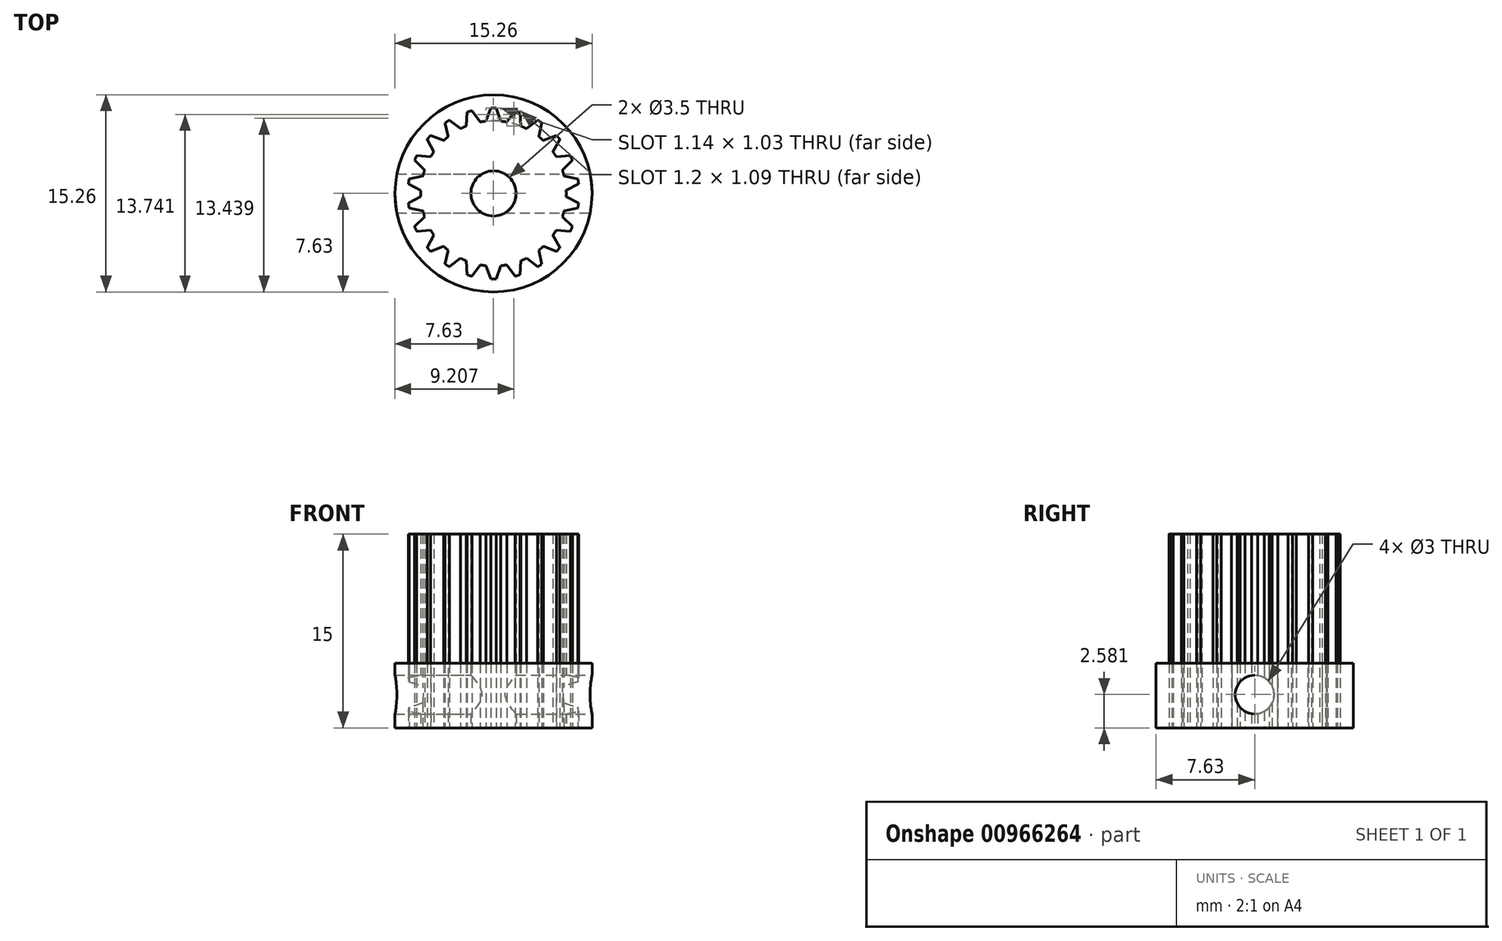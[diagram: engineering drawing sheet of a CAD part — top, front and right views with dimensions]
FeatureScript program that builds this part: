
annotation { "Feature Type Name" : "Feature", "Feature Type Description" : "" }
export const myFeature = defineFeature(function(context is Context, id is Id, definition is map)
    precondition{}
    {
        {
            var Q0;
            Q0=qCreatedBy(makeId("Top.planeOp"),FACE);
            var sketch = newSketch(context, id + "F0", { "sketchPlane" : qUnion([Q0])});
            skCircle(sketch, "E0", {"center": v(0, 0) * mm, "radius": 5.62 * mm});
            skCircle(sketch, "E1", {"center": v(0, 0) * mm, "radius": 7.12 * mm});
            skLineSegment(sketch, "E2", {"start": v(-0.01, 7.12) * mm, "end": v(-0.2, 6.62) * mm});
            skLineSegment(sketch, "E3", {"start": v(0.01, 7.12) * mm, "end": v(0.57, 5.6) * mm});
            skLineSegment(sketch, "E4.1.0", {"start": v(-2.02, 6.83) * mm, "end": v(-2.12, 5.2) * mm});
            skLineSegment(sketch, "E4.1.1", {"start": v(-2, 6.84) * mm, "end": v(-1.03, 5.53) * mm});
            skLineSegment(sketch, "E4.2.0", {"start": v(-3.86, 5.99) * mm, "end": v(-3.5, 4.4) * mm});
            skLineSegment(sketch, "E4.2.1", {"start": v(-3.84, 6) * mm, "end": v(-2.55, 5.02) * mm});
            skLineSegment(sketch, "E4.3.0", {"start": v(-5.4, 4.66) * mm, "end": v(-4.6, 3.23) * mm});
            skLineSegment(sketch, "E4.3.1", {"start": v(-5.38, 4.68) * mm, "end": v(-3.86, 4.1) * mm});
            skLineSegment(sketch, "E4.4.0", {"start": v(-6.49, 2.95) * mm, "end": v(-5.33, 1.8) * mm});
            skLineSegment(sketch, "E4.4.1", {"start": v(-6.48, 2.97) * mm, "end": v(-4.85, 2.84) * mm});
            skLineSegment(sketch, "E4.5.0", {"start": v(-7.05, 1) * mm, "end": v(-5.62, 0.23) * mm});
            skLineSegment(sketch, "E4.5.1", {"start": v(-7.05, 1.03) * mm, "end": v(-5.46, 1.36) * mm});
            skLineSegment(sketch, "E4.6.0", {"start": v(-7.05, -1.03) * mm, "end": v(-5.46, -1.36) * mm});
            skLineSegment(sketch, "E4.6.1", {"start": v(-7.05, -1) * mm, "end": v(-5.62, -0.23) * mm});
            skLineSegment(sketch, "E4.7.0", {"start": v(-6.48, -2.97) * mm, "end": v(-4.85, -2.84) * mm});
            skLineSegment(sketch, "E4.7.1", {"start": v(-6.49, -2.95) * mm, "end": v(-5.33, -1.8) * mm});
            skLineSegment(sketch, "E4.8.0", {"start": v(-5.38, -4.68) * mm, "end": v(-3.86, -4.1) * mm});
            skLineSegment(sketch, "E4.8.1", {"start": v(-5.4, -4.66) * mm, "end": v(-4.6, -3.23) * mm});
            skLineSegment(sketch, "E4.9.0", {"start": v(-3.84, -6) * mm, "end": v(-2.55, -5.02) * mm});
            skLineSegment(sketch, "E4.9.1", {"start": v(-3.86, -5.99) * mm, "end": v(-3.5, -4.4) * mm});
            skLineSegment(sketch, "E5.2.10.0", {"start": v(-2, -6.84) * mm, "end": v(-1.03, -5.53) * mm});
            skLineSegment(sketch, "E5.3.10.0", {"start": v(-2.02, -6.83) * mm, "end": v(-2.12, -5.2) * mm});
            skLineSegment(sketch, "E5.2.11.0", {"start": v(0.01, -7.12) * mm, "end": v(0.57, -5.6) * mm});
            skLineSegment(sketch, "E5.3.11.0", {"start": v(-0.01, -7.12) * mm, "end": v(-0.57, -5.6) * mm});
            skLineSegment(sketch, "E5.2.12.0", {"start": v(2.02, -6.83) * mm, "end": v(2.12, -5.2) * mm});
            skLineSegment(sketch, "E5.3.12.0", {"start": v(2, -6.84) * mm, "end": v(1.03, -5.53) * mm});
            skLineSegment(sketch, "E5.2.13.0", {"start": v(3.86, -5.99) * mm, "end": v(3.5, -4.4) * mm});
            skLineSegment(sketch, "E5.3.13.0", {"start": v(3.84, -6) * mm, "end": v(2.55, -5.02) * mm});
            skLineSegment(sketch, "E5.2.14.0", {"start": v(5.4, -4.66) * mm, "end": v(4.6, -3.23) * mm});
            skLineSegment(sketch, "E5.3.14.0", {"start": v(5.38, -4.68) * mm, "end": v(3.86, -4.1) * mm});
            skLineSegment(sketch, "E5.2.15.0", {"start": v(6.49, -2.95) * mm, "end": v(5.33, -1.8) * mm});
            skLineSegment(sketch, "E5.3.15.0", {"start": v(6.48, -2.97) * mm, "end": v(4.85, -2.84) * mm});
            skLineSegment(sketch, "E5.2.16.0", {"start": v(7.05, -1) * mm, "end": v(5.62, -0.23) * mm});
            skLineSegment(sketch, "E5.3.16.0", {"start": v(7.05, -1.03) * mm, "end": v(5.46, -1.36) * mm});
            skLineSegment(sketch, "E5.2.17.0", {"start": v(7.05, 1.03) * mm, "end": v(5.46, 1.36) * mm});
            skLineSegment(sketch, "E5.3.17.0", {"start": v(7.05, 1) * mm, "end": v(5.62, 0.23) * mm});
            skLineSegment(sketch, "E5.2.18.0", {"start": v(6.48, 2.97) * mm, "end": v(4.85, 2.84) * mm});
            skLineSegment(sketch, "E5.3.18.0", {"start": v(6.49, 2.95) * mm, "end": v(5.33, 1.8) * mm});
            skLineSegment(sketch, "E5.2.19.0", {"start": v(5.38, 4.68) * mm, "end": v(3.86, 4.1) * mm});
            skLineSegment(sketch, "E5.3.19.0", {"start": v(5.4, 4.66) * mm, "end": v(4.6, 3.23) * mm});
            skLineSegment(sketch, "E6.2.20.0", {"start": v(3.84, 6) * mm, "end": v(2.55, 5.02) * mm});
            skLineSegment(sketch, "E6.3.20.0", {"start": v(3.86, 5.99) * mm, "end": v(3.5, 4.4) * mm});
            skCircle(sketch, "E7", {"center": v(0, 0) * mm, "radius": 1.75 * mm});
            skCircle(sketch, "E8", {"center": v(0, 0) * mm, "radius": 7.62 * mm});
            skLineSegment(sketch, "E9.2.21.0", {"start": v(2, 6.84) * mm, "end": v(1.03, 5.53) * mm});
            skLineSegment(sketch, "E9.3.21.0", {"start": v(2.02, 6.83) * mm, "end": v(2.12, 5.2) * mm});
            skLineSegment(sketch, "E10", {"start": v(-0.2, 6.62) * mm, "end": v(-0.57, 5.6) * mm});
            skArc(sketch, "E11", {"start": v(0.2, 6.62) * mm, "mid": v(0, 6.63) * mm, "end": v(-0.2, 6.62) * mm});
            skArc(sketch, "E12", {"start": v(-0.2, 6.62) * mm, "mid": v(0, -6.63) * mm, "end": v(0.2, 6.62) * mm});
            skSolve(sketch);
        }
        {
            var Q0;
            Q0=makeQuery(id+"F0.imprint","IMPRINT",FACE,{"disambiguationData":[TD([[makeQuery(id+"F0.imprint","IMPRINT",EDGE,{"derivedFrom":sQuery(id+"F0.wireOp",EDGE,"E7")}),-1.0]])]});
            var Q1;
            {var subQ3=sQuery(id+"F0.wireOp",EDGE,"E10");Q1=makeQuery(id+"F0.imprint","IMPRINT",FACE,{"disambiguationData":[TD([[makeQuery(id+"F0.imprint","IMPRINT",EDGE,{"derivedFrom":subQ3}),1.0]])]});}
            var Q2;
            {var subQ0=sQuery(id+"F0.wireOp",EDGE,"E9.2.21.0");var subQ1=sQuery(id+"F0.wireOp",EDGE,"E0");var subQ2=makeQuery(id+"F0.imprint","INTERSECT",VERTEX,{"derivedFrom":[subQ1,subQ0]});Q2=makeQuery(id+"F0.imprint","IMPRINT",FACE,{"disambiguationData":[TD([[makeQuery(id+"F0.imprint","IMPRINT",EDGE,{"disambiguationData":[TD([[subQ2,1.0]])],"derivedFrom":subQ1}),-1.0]])]});}
            var Q3;
            {var subQ0=sQuery(id+"F0.wireOp",EDGE,"E6.2.20.0");var subQ1=sQuery(id+"F0.wireOp",EDGE,"E0");var subQ2=makeQuery(id+"F0.imprint","INTERSECT",VERTEX,{"derivedFrom":[subQ1,subQ0]});Q3=makeQuery(id+"F0.imprint","IMPRINT",FACE,{"disambiguationData":[TD([[makeQuery(id+"F0.imprint","IMPRINT",EDGE,{"disambiguationData":[TD([[subQ2,1.0]])],"derivedFrom":subQ1}),-1.0]])]});}
            var Q4;
            {var subQ0=sQuery(id+"F0.wireOp",EDGE,"E5.2.19.0");var subQ1=sQuery(id+"F0.wireOp",EDGE,"E0");var subQ2=makeQuery(id+"F0.imprint","INTERSECT",VERTEX,{"derivedFrom":[subQ1,subQ0]});Q4=makeQuery(id+"F0.imprint","IMPRINT",FACE,{"disambiguationData":[TD([[makeQuery(id+"F0.imprint","IMPRINT",EDGE,{"disambiguationData":[TD([[subQ2,1.0]])],"derivedFrom":subQ1}),-1.0]])]});}
            var Q5;
            {var subQ0=sQuery(id+"F0.wireOp",EDGE,"E5.2.18.0");var subQ1=sQuery(id+"F0.wireOp",EDGE,"E0");var subQ2=makeQuery(id+"F0.imprint","INTERSECT",VERTEX,{"derivedFrom":[subQ1,subQ0]});Q5=makeQuery(id+"F0.imprint","IMPRINT",FACE,{"disambiguationData":[TD([[makeQuery(id+"F0.imprint","IMPRINT",EDGE,{"disambiguationData":[TD([[subQ2,1.0]])],"derivedFrom":subQ1}),-1.0]])]});}
            var Q6;
            {var subQ0=sQuery(id+"F0.wireOp",EDGE,"E5.2.17.0");var subQ1=sQuery(id+"F0.wireOp",EDGE,"E0");var subQ2=makeQuery(id+"F0.imprint","INTERSECT",VERTEX,{"derivedFrom":[subQ1,subQ0]});Q6=makeQuery(id+"F0.imprint","IMPRINT",FACE,{"disambiguationData":[TD([[makeQuery(id+"F0.imprint","IMPRINT",EDGE,{"disambiguationData":[TD([[subQ2,1.0]])],"derivedFrom":subQ1}),-1.0]])]});}
            var Q7;
            {var subQ0=sQuery(id+"F0.wireOp",EDGE,"E5.2.16.0");var subQ1=sQuery(id+"F0.wireOp",EDGE,"E0");var subQ2=makeQuery(id+"F0.imprint","INTERSECT",VERTEX,{"derivedFrom":[subQ1,subQ0]});Q7=makeQuery(id+"F0.imprint","IMPRINT",FACE,{"disambiguationData":[TD([[makeQuery(id+"F0.imprint","IMPRINT",EDGE,{"disambiguationData":[TD([[subQ2,1.0]])],"derivedFrom":subQ1}),-1.0]])]});}
            var Q8;
            {var subQ0=sQuery(id+"F0.wireOp",EDGE,"E5.2.15.0");var subQ1=sQuery(id+"F0.wireOp",EDGE,"E0");var subQ2=makeQuery(id+"F0.imprint","INTERSECT",VERTEX,{"derivedFrom":[subQ1,subQ0]});Q8=makeQuery(id+"F0.imprint","IMPRINT",FACE,{"disambiguationData":[TD([[makeQuery(id+"F0.imprint","IMPRINT",EDGE,{"disambiguationData":[TD([[subQ2,1.0]])],"derivedFrom":subQ1}),-1.0]])]});}
            var Q9;
            {var subQ0=sQuery(id+"F0.wireOp",EDGE,"E5.2.14.0");var subQ1=sQuery(id+"F0.wireOp",EDGE,"E0");var subQ2=makeQuery(id+"F0.imprint","INTERSECT",VERTEX,{"derivedFrom":[subQ1,subQ0]});Q9=makeQuery(id+"F0.imprint","IMPRINT",FACE,{"disambiguationData":[TD([[makeQuery(id+"F0.imprint","IMPRINT",EDGE,{"disambiguationData":[TD([[subQ2,1.0]])],"derivedFrom":subQ1}),-1.0]])]});}
            var Q10;
            {var subQ0=sQuery(id+"F0.wireOp",EDGE,"E5.2.13.0");var subQ1=sQuery(id+"F0.wireOp",EDGE,"E0");var subQ2=makeQuery(id+"F0.imprint","INTERSECT",VERTEX,{"derivedFrom":[subQ1,subQ0]});Q10=makeQuery(id+"F0.imprint","IMPRINT",FACE,{"disambiguationData":[TD([[makeQuery(id+"F0.imprint","IMPRINT",EDGE,{"disambiguationData":[TD([[subQ2,1.0]])],"derivedFrom":subQ1}),-1.0]])]});}
            var Q11;
            {var subQ0=sQuery(id+"F0.wireOp",EDGE,"E5.2.12.0");var subQ1=sQuery(id+"F0.wireOp",EDGE,"E0");var subQ2=makeQuery(id+"F0.imprint","INTERSECT",VERTEX,{"derivedFrom":[subQ1,subQ0]});Q11=makeQuery(id+"F0.imprint","IMPRINT",FACE,{"disambiguationData":[TD([[makeQuery(id+"F0.imprint","IMPRINT",EDGE,{"disambiguationData":[TD([[subQ2,1.0]])],"derivedFrom":subQ1}),-1.0]])]});}
            var Q12;
            {var subQ0=sQuery(id+"F0.wireOp",EDGE,"E5.2.11.0");var subQ1=sQuery(id+"F0.wireOp",EDGE,"E0");var subQ2=makeQuery(id+"F0.imprint","INTERSECT",VERTEX,{"derivedFrom":[subQ1,subQ0]});Q12=makeQuery(id+"F0.imprint","IMPRINT",FACE,{"disambiguationData":[TD([[makeQuery(id+"F0.imprint","IMPRINT",EDGE,{"disambiguationData":[TD([[subQ2,1.0]])],"derivedFrom":subQ1}),-1.0]])]});}
            var Q13;
            {var subQ0=sQuery(id+"F0.wireOp",EDGE,"E5.2.10.0");var subQ1=sQuery(id+"F0.wireOp",EDGE,"E0");var subQ2=makeQuery(id+"F0.imprint","INTERSECT",VERTEX,{"derivedFrom":[subQ1,subQ0]});Q13=makeQuery(id+"F0.imprint","IMPRINT",FACE,{"disambiguationData":[TD([[makeQuery(id+"F0.imprint","IMPRINT",EDGE,{"disambiguationData":[TD([[subQ2,1.0]])],"derivedFrom":subQ1}),-1.0]])]});}
            var Q14;
            {var subQ0=sQuery(id+"F0.wireOp",EDGE,"E4.9.0");var subQ1=sQuery(id+"F0.wireOp",EDGE,"E0");var subQ2=makeQuery(id+"F0.imprint","INTERSECT",VERTEX,{"derivedFrom":[subQ1,subQ0]});Q14=makeQuery(id+"F0.imprint","IMPRINT",FACE,{"disambiguationData":[TD([[makeQuery(id+"F0.imprint","IMPRINT",EDGE,{"disambiguationData":[TD([[subQ2,1.0]])],"derivedFrom":subQ1}),-1.0]])]});}
            var Q15;
            {var subQ0=sQuery(id+"F0.wireOp",EDGE,"E4.8.0");var subQ1=sQuery(id+"F0.wireOp",EDGE,"E0");var subQ2=makeQuery(id+"F0.imprint","INTERSECT",VERTEX,{"derivedFrom":[subQ1,subQ0]});Q15=makeQuery(id+"F0.imprint","IMPRINT",FACE,{"disambiguationData":[TD([[makeQuery(id+"F0.imprint","IMPRINT",EDGE,{"disambiguationData":[TD([[subQ2,1.0]])],"derivedFrom":subQ1}),-1.0]])]});}
            var Q16;
            {var subQ0=sQuery(id+"F0.wireOp",EDGE,"E4.7.0");var subQ1=sQuery(id+"F0.wireOp",EDGE,"E0");var subQ2=makeQuery(id+"F0.imprint","INTERSECT",VERTEX,{"derivedFrom":[subQ1,subQ0]});Q16=makeQuery(id+"F0.imprint","IMPRINT",FACE,{"disambiguationData":[TD([[makeQuery(id+"F0.imprint","IMPRINT",EDGE,{"disambiguationData":[TD([[subQ2,1.0]])],"derivedFrom":subQ1}),-1.0]])]});}
            var Q17;
            {var subQ0=sQuery(id+"F0.wireOp",EDGE,"E4.6.0");var subQ1=sQuery(id+"F0.wireOp",EDGE,"E0");var subQ2=makeQuery(id+"F0.imprint","INTERSECT",VERTEX,{"derivedFrom":[subQ1,subQ0]});Q17=makeQuery(id+"F0.imprint","IMPRINT",FACE,{"disambiguationData":[TD([[makeQuery(id+"F0.imprint","IMPRINT",EDGE,{"disambiguationData":[TD([[subQ2,1.0]])],"derivedFrom":subQ1}),-1.0]])]});}
            var Q18;
            {var subQ0=sQuery(id+"F0.wireOp",EDGE,"E4.5.0");var subQ1=sQuery(id+"F0.wireOp",EDGE,"E0");var subQ2=makeQuery(id+"F0.imprint","INTERSECT",VERTEX,{"derivedFrom":[subQ1,subQ0]});Q18=makeQuery(id+"F0.imprint","IMPRINT",FACE,{"disambiguationData":[TD([[makeQuery(id+"F0.imprint","IMPRINT",EDGE,{"disambiguationData":[TD([[subQ2,1.0]])],"derivedFrom":subQ1}),-1.0]])]});}
            var Q19;
            {var subQ0=sQuery(id+"F0.wireOp",EDGE,"E4.4.0");var subQ1=sQuery(id+"F0.wireOp",EDGE,"E0");var subQ2=makeQuery(id+"F0.imprint","INTERSECT",VERTEX,{"derivedFrom":[subQ1,subQ0]});Q19=makeQuery(id+"F0.imprint","IMPRINT",FACE,{"disambiguationData":[TD([[makeQuery(id+"F0.imprint","IMPRINT",EDGE,{"disambiguationData":[TD([[subQ2,1.0]])],"derivedFrom":subQ1}),-1.0]])]});}
            var Q20;
            {var subQ0=sQuery(id+"F0.wireOp",EDGE,"E4.3.0");var subQ1=sQuery(id+"F0.wireOp",EDGE,"E0");var subQ2=makeQuery(id+"F0.imprint","INTERSECT",VERTEX,{"derivedFrom":[subQ1,subQ0]});Q20=makeQuery(id+"F0.imprint","IMPRINT",FACE,{"disambiguationData":[TD([[makeQuery(id+"F0.imprint","IMPRINT",EDGE,{"disambiguationData":[TD([[subQ2,1.0]])],"derivedFrom":subQ1}),-1.0]])]});}
            var Q21;
            {var subQ0=sQuery(id+"F0.wireOp",EDGE,"E4.2.0");var subQ1=sQuery(id+"F0.wireOp",EDGE,"E0");var subQ2=makeQuery(id+"F0.imprint","INTERSECT",VERTEX,{"derivedFrom":[subQ1,subQ0]});Q21=makeQuery(id+"F0.imprint","IMPRINT",FACE,{"disambiguationData":[TD([[makeQuery(id+"F0.imprint","IMPRINT",EDGE,{"disambiguationData":[TD([[subQ2,1.0]])],"derivedFrom":subQ1}),-1.0]])]});}
            var Q22;
            {var subQ0=sQuery(id+"F0.wireOp",EDGE,"E4.1.0");var subQ1=sQuery(id+"F0.wireOp",EDGE,"E0");var subQ2=makeQuery(id+"F0.imprint","INTERSECT",VERTEX,{"derivedFrom":[subQ1,subQ0]});Q22=makeQuery(id+"F0.imprint","IMPRINT",FACE,{"disambiguationData":[TD([[makeQuery(id+"F0.imprint","IMPRINT",EDGE,{"disambiguationData":[TD([[subQ2,1.0]])],"derivedFrom":subQ1}),-1.0]])]});}
            extrude(context, id + "F1", {"entities" : qUnion([Q0, Q1, Q2, Q3, Q4, Q5, Q6, Q7, Q8, Q9, Q10, Q11, Q12, Q13, Q14, Q15, Q16, Q17, Q18, Q19, Q20, Q21, Q22]), "depth" : 15 * mm, "offsetDistance" : 25 * mm});
        }
        {
            var Q0;
            Q0=makeQuery(id+"F0.imprint","IMPRINT",FACE,{"disambiguationData":[TD([[makeQuery(id+"F0.imprint","IMPRINT",EDGE,{"derivedFrom":sQuery(id+"F0.wireOp",EDGE,"E8")}),1.0]])]});
            var Q1;
            {var subQ0=sQuery(id+"F0.wireOp",EDGE,"E4.3.0");Q1=makeQuery(id+"F0.imprint","IMPRINT",FACE,{"disambiguationData":[TD([[makeQuery(id+"F0.imprint","IMPRINT",EDGE,{"derivedFrom":subQ0}),1.0]])]});}
            var Q2;
            {var subQ0=sQuery(id+"F0.wireOp",EDGE,"E5.2.14.0");Q2=makeQuery(id+"F0.imprint","IMPRINT",FACE,{"disambiguationData":[TD([[makeQuery(id+"F0.imprint","IMPRINT",EDGE,{"derivedFrom":subQ0}),-1.0]])]});}
            var Q3;
            {var subQ0=sQuery(id+"F0.wireOp",EDGE,"E3");Q3=makeQuery(id+"F0.imprint","IMPRINT",FACE,{"disambiguationData":[TD([[makeQuery(id+"F0.imprint","IMPRINT",EDGE,{"derivedFrom":subQ0}),1.0]])]});}
            var Q4;
            {var subQ0=sQuery(id+"F0.wireOp",EDGE,"E5.2.18.0");Q4=makeQuery(id+"F0.imprint","IMPRINT",FACE,{"disambiguationData":[TD([[makeQuery(id+"F0.imprint","IMPRINT",EDGE,{"derivedFrom":subQ0}),-1.0]])]});}
            var Q5;
            {var subQ0=sQuery(id+"F0.wireOp",EDGE,"E5.2.12.0");Q5=makeQuery(id+"F0.imprint","IMPRINT",FACE,{"disambiguationData":[TD([[makeQuery(id+"F0.imprint","IMPRINT",EDGE,{"derivedFrom":subQ0}),1.0]])]});}
            var Q6;
            {var subQ0=sQuery(id+"F0.wireOp",EDGE,"E4.6.0");Q6=makeQuery(id+"F0.imprint","IMPRINT",FACE,{"disambiguationData":[TD([[makeQuery(id+"F0.imprint","IMPRINT",EDGE,{"derivedFrom":subQ0}),1.0]])]});}
            var Q7;
            {var subQ0=sQuery(id+"F0.wireOp",EDGE,"E4.7.0");Q7=makeQuery(id+"F0.imprint","IMPRINT",FACE,{"disambiguationData":[TD([[makeQuery(id+"F0.imprint","IMPRINT",EDGE,{"derivedFrom":subQ0}),1.0]])]});}
            var Q8;
            {var subQ0=sQuery(id+"F0.wireOp",EDGE,"E5.2.19.0");Q8=makeQuery(id+"F0.imprint","IMPRINT",FACE,{"disambiguationData":[TD([[makeQuery(id+"F0.imprint","IMPRINT",EDGE,{"derivedFrom":subQ0}),1.0]])]});}
            var Q9;
            {var subQ0=sQuery(id+"F0.wireOp",EDGE,"E5.2.17.0");Q9=makeQuery(id+"F0.imprint","IMPRINT",FACE,{"disambiguationData":[TD([[makeQuery(id+"F0.imprint","IMPRINT",EDGE,{"derivedFrom":subQ0}),-1.0]])]});}
            var Q10;
            {var subQ0=sQuery(id+"F0.wireOp",EDGE,"E5.2.10.0");Q10=makeQuery(id+"F0.imprint","IMPRINT",FACE,{"disambiguationData":[TD([[makeQuery(id+"F0.imprint","IMPRINT",EDGE,{"derivedFrom":subQ0}),1.0]])]});}
            var Q11;
            {var subQ0=sQuery(id+"F0.wireOp",EDGE,"E5.2.15.0");Q11=makeQuery(id+"F0.imprint","IMPRINT",FACE,{"disambiguationData":[TD([[makeQuery(id+"F0.imprint","IMPRINT",EDGE,{"derivedFrom":subQ0}),1.0]])]});}
            var Q12;
            {var subQ0=sQuery(id+"F0.wireOp",EDGE,"E4.1.0");Q12=makeQuery(id+"F0.imprint","IMPRINT",FACE,{"disambiguationData":[TD([[makeQuery(id+"F0.imprint","IMPRINT",EDGE,{"derivedFrom":subQ0}),-1.0]])]});}
            var Q13;
            {var subQ0=sQuery(id+"F0.wireOp",EDGE,"E5.2.11.0");Q13=makeQuery(id+"F0.imprint","IMPRINT",FACE,{"disambiguationData":[TD([[makeQuery(id+"F0.imprint","IMPRINT",EDGE,{"derivedFrom":subQ0}),-1.0]])]});}
            var Q14;
            {var subQ0=sQuery(id+"F0.wireOp",EDGE,"E6.2.20.0");Q14=makeQuery(id+"F0.imprint","IMPRINT",FACE,{"disambiguationData":[TD([[makeQuery(id+"F0.imprint","IMPRINT",EDGE,{"derivedFrom":subQ0}),1.0]])]});}
            var Q15;
            {var subQ0=sQuery(id+"F0.wireOp",EDGE,"E4.6.0");Q15=makeQuery(id+"F0.imprint","IMPRINT",FACE,{"disambiguationData":[TD([[makeQuery(id+"F0.imprint","IMPRINT",EDGE,{"derivedFrom":subQ0}),-1.0]])]});}
            var Q16;
            {var subQ0=sQuery(id+"F0.wireOp",EDGE,"E5.2.11.0");Q16=makeQuery(id+"F0.imprint","IMPRINT",FACE,{"disambiguationData":[TD([[makeQuery(id+"F0.imprint","IMPRINT",EDGE,{"derivedFrom":subQ0}),1.0]])]});}
            var Q17;
            {var subQ0=sQuery(id+"F0.wireOp",EDGE,"E4.8.0");Q17=makeQuery(id+"F0.imprint","IMPRINT",FACE,{"disambiguationData":[TD([[makeQuery(id+"F0.imprint","IMPRINT",EDGE,{"derivedFrom":subQ0}),1.0]])]});}
            var Q18;
            {var subQ0=sQuery(id+"F0.wireOp",EDGE,"E5.2.19.0");Q18=makeQuery(id+"F0.imprint","IMPRINT",FACE,{"disambiguationData":[TD([[makeQuery(id+"F0.imprint","IMPRINT",EDGE,{"derivedFrom":subQ0}),-1.0]])]});}
            var Q19;
            {var subQ0=sQuery(id+"F0.wireOp",EDGE,"E5.2.15.0");Q19=makeQuery(id+"F0.imprint","IMPRINT",FACE,{"disambiguationData":[TD([[makeQuery(id+"F0.imprint","IMPRINT",EDGE,{"derivedFrom":subQ0}),-1.0]])]});}
            var Q20;
            {var subQ0=sQuery(id+"F0.wireOp",EDGE,"E5.2.10.0");Q20=makeQuery(id+"F0.imprint","IMPRINT",FACE,{"disambiguationData":[TD([[makeQuery(id+"F0.imprint","IMPRINT",EDGE,{"derivedFrom":subQ0}),-1.0]])]});}
            var Q21;
            {var subQ0=sQuery(id+"F0.wireOp",EDGE,"E4.2.0");Q21=makeQuery(id+"F0.imprint","IMPRINT",FACE,{"disambiguationData":[TD([[makeQuery(id+"F0.imprint","IMPRINT",EDGE,{"derivedFrom":subQ0}),-1.0]])]});}
            var Q22;
            {var subQ0=sQuery(id+"F0.wireOp",EDGE,"E4.7.0");Q22=makeQuery(id+"F0.imprint","IMPRINT",FACE,{"disambiguationData":[TD([[makeQuery(id+"F0.imprint","IMPRINT",EDGE,{"derivedFrom":subQ0}),-1.0]])]});}
            var Q23;
            {var subQ0=sQuery(id+"F0.wireOp",EDGE,"E4.4.0");Q23=makeQuery(id+"F0.imprint","IMPRINT",FACE,{"disambiguationData":[TD([[makeQuery(id+"F0.imprint","IMPRINT",EDGE,{"derivedFrom":subQ0}),1.0]])]});}
            var Q24;
            {var subQ0=sQuery(id+"F0.wireOp",EDGE,"E5.2.13.0");Q24=makeQuery(id+"F0.imprint","IMPRINT",FACE,{"disambiguationData":[TD([[makeQuery(id+"F0.imprint","IMPRINT",EDGE,{"derivedFrom":subQ0}),1.0]])]});}
            var Q25;
            {var subQ0=sQuery(id+"F0.wireOp",EDGE,"E5.2.17.0");Q25=makeQuery(id+"F0.imprint","IMPRINT",FACE,{"disambiguationData":[TD([[makeQuery(id+"F0.imprint","IMPRINT",EDGE,{"derivedFrom":subQ0}),1.0]])]});}
            var Q26;
            {var subQ0=sQuery(id+"F0.wireOp",EDGE,"E4.5.0");Q26=makeQuery(id+"F0.imprint","IMPRINT",FACE,{"disambiguationData":[TD([[makeQuery(id+"F0.imprint","IMPRINT",EDGE,{"derivedFrom":subQ0}),1.0]])]});}
            var Q27;
            {var subQ0=sQuery(id+"F0.wireOp",EDGE,"E2");Q27=makeQuery(id+"F0.imprint","IMPRINT",FACE,{"disambiguationData":[TD([[makeQuery(id+"F0.imprint","IMPRINT",EDGE,{"derivedFrom":subQ0}),1.0]])]});}
            var Q28;
            {var subQ0=sQuery(id+"F0.wireOp",EDGE,"E4.9.0");Q28=makeQuery(id+"F0.imprint","IMPRINT",FACE,{"disambiguationData":[TD([[makeQuery(id+"F0.imprint","IMPRINT",EDGE,{"derivedFrom":subQ0}),1.0]])]});}
            var Q29;
            {var subQ0=sQuery(id+"F0.wireOp",EDGE,"E5.2.18.0");Q29=makeQuery(id+"F0.imprint","IMPRINT",FACE,{"disambiguationData":[TD([[makeQuery(id+"F0.imprint","IMPRINT",EDGE,{"derivedFrom":subQ0}),1.0]])]});}
            var Q30;
            {var subQ0=sQuery(id+"F0.wireOp",EDGE,"E4.5.0");Q30=makeQuery(id+"F0.imprint","IMPRINT",FACE,{"disambiguationData":[TD([[makeQuery(id+"F0.imprint","IMPRINT",EDGE,{"derivedFrom":subQ0}),-1.0]])]});}
            var Q31;
            {var subQ0=sQuery(id+"F0.wireOp",EDGE,"E4.4.0");Q31=makeQuery(id+"F0.imprint","IMPRINT",FACE,{"disambiguationData":[TD([[makeQuery(id+"F0.imprint","IMPRINT",EDGE,{"derivedFrom":subQ0}),-1.0]])]});}
            var Q32;
            {var subQ0=sQuery(id+"F0.wireOp",EDGE,"E4.3.0");Q32=makeQuery(id+"F0.imprint","IMPRINT",FACE,{"disambiguationData":[TD([[makeQuery(id+"F0.imprint","IMPRINT",EDGE,{"derivedFrom":subQ0}),-1.0]])]});}
            var Q33;
            {var subQ0=sQuery(id+"F0.wireOp",EDGE,"E5.2.16.0");Q33=makeQuery(id+"F0.imprint","IMPRINT",FACE,{"disambiguationData":[TD([[makeQuery(id+"F0.imprint","IMPRINT",EDGE,{"derivedFrom":subQ0}),1.0]])]});}
            var Q34;
            {var subQ0=sQuery(id+"F0.wireOp",EDGE,"E2");Q34=makeQuery(id+"F0.imprint","IMPRINT",FACE,{"disambiguationData":[TD([[makeQuery(id+"F0.imprint","IMPRINT",EDGE,{"derivedFrom":subQ0}),-1.0]])]});}
            var Q35;
            {var subQ0=sQuery(id+"F0.wireOp",EDGE,"E4.8.0");Q35=makeQuery(id+"F0.imprint","IMPRINT",FACE,{"disambiguationData":[TD([[makeQuery(id+"F0.imprint","IMPRINT",EDGE,{"derivedFrom":subQ0}),-1.0]])]});}
            var Q36;
            {var subQ0=sQuery(id+"F0.wireOp",EDGE,"E4.2.0");Q36=makeQuery(id+"F0.imprint","IMPRINT",FACE,{"disambiguationData":[TD([[makeQuery(id+"F0.imprint","IMPRINT",EDGE,{"derivedFrom":subQ0}),1.0]])]});}
            var Q37;
            {var subQ0=sQuery(id+"F0.wireOp",EDGE,"E4.1.0");Q37=makeQuery(id+"F0.imprint","IMPRINT",FACE,{"disambiguationData":[TD([[makeQuery(id+"F0.imprint","IMPRINT",EDGE,{"derivedFrom":subQ0}),1.0]])]});}
            var Q38;
            {var subQ0=sQuery(id+"F0.wireOp",EDGE,"E5.2.12.0");Q38=makeQuery(id+"F0.imprint","IMPRINT",FACE,{"disambiguationData":[TD([[makeQuery(id+"F0.imprint","IMPRINT",EDGE,{"derivedFrom":subQ0}),-1.0]])]});}
            var Q39;
            {var subQ0=sQuery(id+"F0.wireOp",EDGE,"E5.2.13.0");Q39=makeQuery(id+"F0.imprint","IMPRINT",FACE,{"disambiguationData":[TD([[makeQuery(id+"F0.imprint","IMPRINT",EDGE,{"derivedFrom":subQ0}),-1.0]])]});}
            var Q40;
            {var subQ0=sQuery(id+"F0.wireOp",EDGE,"E5.2.16.0");Q40=makeQuery(id+"F0.imprint","IMPRINT",FACE,{"disambiguationData":[TD([[makeQuery(id+"F0.imprint","IMPRINT",EDGE,{"derivedFrom":subQ0}),-1.0]])]});}
            var Q41;
            {var subQ0=sQuery(id+"F0.wireOp",EDGE,"E4.9.0");Q41=makeQuery(id+"F0.imprint","IMPRINT",FACE,{"disambiguationData":[TD([[makeQuery(id+"F0.imprint","IMPRINT",EDGE,{"derivedFrom":subQ0}),-1.0]])]});}
            var Q42;
            {var subQ0=sQuery(id+"F0.wireOp",EDGE,"E5.2.14.0");Q42=makeQuery(id+"F0.imprint","IMPRINT",FACE,{"disambiguationData":[TD([[makeQuery(id+"F0.imprint","IMPRINT",EDGE,{"derivedFrom":subQ0}),1.0]])]});}
            var Q43;
            Q43=makeQuery(id+"F0.imprint","IMPRINT",FACE,{"disambiguationData":[TD([[makeQuery(id+"F0.imprint","IMPRINT",EDGE,{"derivedFrom":sQuery(id+"F0.wireOp",EDGE,"E7")}),-1.0]])]});
            var Q44;
            {var subQ3=sQuery(id+"F0.wireOp",EDGE,"E10");Q44=makeQuery(id+"F0.imprint","IMPRINT",FACE,{"disambiguationData":[TD([[makeQuery(id+"F0.imprint","IMPRINT",EDGE,{"derivedFrom":subQ3}),-1.0]])]});}
            var Q45;
            {var subQ0=sQuery(id+"F0.wireOp",EDGE,"E6.2.20.0");var subQ1=sQuery(id+"F0.wireOp",EDGE,"E0");var subQ2=makeQuery(id+"F0.imprint","INTERSECT",VERTEX,{"derivedFrom":[subQ1,subQ0]});Q45=makeQuery(id+"F0.imprint","IMPRINT",FACE,{"disambiguationData":[TD([[makeQuery(id+"F0.imprint","IMPRINT",EDGE,{"disambiguationData":[TD([[subQ2,-1.0]])],"derivedFrom":subQ1}),-1.0]])]});}
            var Q46;
            {var subQ0=sQuery(id+"F0.wireOp",EDGE,"E6.2.20.0");var subQ1=sQuery(id+"F0.wireOp",EDGE,"E1");var subQ2=makeQuery(id+"F0.imprint","INTERSECT",VERTEX,{"derivedFrom":[subQ1,subQ0]});Q46=makeQuery(id+"F0.imprint","IMPRINT",FACE,{"disambiguationData":[TD([[makeQuery(id+"F0.imprint","IMPRINT",EDGE,{"disambiguationData":[TD([[subQ2,-1.0]])],"derivedFrom":subQ1}),1.0]])]});}
            var Q47;
            {var subQ0=sQuery(id+"F0.wireOp",EDGE,"E9.2.21.0");var subQ1=sQuery(id+"F0.wireOp",EDGE,"E1");var subQ2=makeQuery(id+"F0.imprint","INTERSECT",VERTEX,{"derivedFrom":[subQ1,subQ0]});Q47=makeQuery(id+"F0.imprint","IMPRINT",FACE,{"disambiguationData":[TD([[makeQuery(id+"F0.imprint","IMPRINT",EDGE,{"disambiguationData":[TD([[subQ2,1.0]])],"derivedFrom":subQ1}),1.0]])]});}
            extrude(context, id + "F2", {"entities" : qUnion([Q0, Q1, Q2, Q3, Q4, Q5, Q6, Q7, Q8, Q9, Q10, Q11, Q12, Q13, Q14, Q15, Q16, Q17, Q18, Q19, Q20, Q21, Q22, Q23, Q24, Q25, Q26, Q27, Q28, Q29, Q30, Q31, Q32, Q33, Q34, Q35, Q36, Q37, Q38, Q39, Q40, Q41, Q42, Q43, Q44, Q45, Q46, Q47]), "depth" : 5 * mm, "offsetDistance" : 25 * mm});
        }
        {
            var Q0;
            Q0=qCreatedBy(makeId("Right.planeOp"),FACE);
            var sketch = newSketch(context, id + "F3", { "sketchPlane" : qUnion([Q0])});
            skCircle(sketch, "E13", {"center": v(0, 2.58) * mm, "radius": 1.5 * mm});
            skLineSegment(sketch, "E14", {"start": v(0, 0) * mm, "end": v(0, 5) * mm, "construction": true});
            skSolve(sketch);
        }
        {
            var Q0;
            Q0 = qSketchRegion(id + "F3", true);
            extrude(context, id + "F4", {"entities" : qUnion([Q0]), "operationType" : NewBodyOperationType.REMOVE, "endBound" : BoundingType.SYMMETRIC, "oppositeDirection" : true, "depth" : 25 * mm, "offsetDistance" : 25 * mm});
        }
    });
